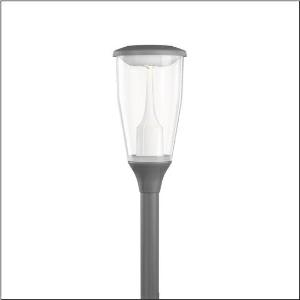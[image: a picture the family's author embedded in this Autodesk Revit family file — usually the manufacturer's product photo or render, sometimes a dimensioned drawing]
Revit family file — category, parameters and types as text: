
# Revit family: dl_11_iq___st1_2a_5xa5575af14hp00022_5e00
name_source: partatom
category: Lighting Fixtures
units: mm (PartAtom-declared; Revit-internal decimal feet)

## family parameters
Cut with Voids When Loaded = No
Host = Face
Light Source = No
Part Type = Normal
Room Calculation Point = No
Round Connector Dimension = Use Diameter
Shared = No

## types (1)
- --- (1 x LED, 4000 lm, 33.6 W, 2200K)
    Apparent Load = 34 VA
    CIE Flux Codes = 33 63 91 94 100
    Color Rendering = 70
    Color Temperature = 2200K
    Default Elevation = 1800 mm
    Description = DL 11 iQ, mast luminaire, Module 540 iQ-SR, primary light control with 3 zone facetted reflector, of plastic, silver coated, highly specular, structured, primary optical cover: cover, of PMMA, transparent, light distribution: ST1.2a, light emission: direct distribution, primary light characteristic: asymmetric, installation type: post-top, LED, High Power LED, rated luminous flux: 4.000lm, luminous efficacy: 119lm/W, light colour: 722, colour temperature: 2200K, control: Street-Remote, Auto-Match, Temp-Guard, Lumen-Switch, Night-Set, Smart-Wire, Light-Fading, Desk-Remote (wireless, voltage-free reading and setting of iQ features in the workshop via application-optimized NFC function/RFID function), optimised constant luminous flux control (CLO 2.0), mains connection: 220..240V, AC, 50/60Hz, connection cable pre-assembled, cable length: 5,5m, start of lifetime: 34W, end of service life: 36W, reduction: 15W, luminaire housing, upper part, of diecast aluminium, coated, Siteco® metallic grey (DB 702S), spigot size: 76mm (post-top), post-top mast mounting element, of diecast aluminium, coated, Siteco® metallic grey (DB 702S), Module 540 iQ-SR, traffic white (RAL 9016), equipment: Power, protection rating (complete): IP66, insulation class (complete): insulation class II (safety insulation), certification: CE, ENEC, ENEC+, VDE, packaging unit: 1 piece

Light Distribution: ST1.2a
    Height = 665 mm
    Lamp = 1 x LED
    Lamp Light Flux = 4000 lm
    Lamp Power = 33.6 W
    Lamp count = 1
    Length = 334 mm
    Luminous efficacy = 119 lm/W
    Manufacturer = Siteco
    ModVariant = No
    Model = 5XA5575AF14HP00022
    Number of Poles = 1
    OnlyDefault = Yes
    Power Factor = 1
    Product Name = DL 11 iQ | ST1.2a
    Product group = mast luminaire | pylon top
    ProductGroupID = 6100
    Protection Class = Protection class II
    Protection Degree = IP 66
    RLX_Detail_Level = 1
    RLX_Emergency_Light_Flux = 0 lm
    RLX_Emergency_Type = 0
    RLX_Emergency_Type_DB = No
    RlxData = <blob elided: 97469 chars, md5=3734c2d8>
    Socket = socket
    Standby Power = 0 W
    System Light Flux = 4000 lm
    System Power = 34 W
    Type Comments = factory setting: luminous flux: 100 % | dim-lin: 254 | 695 mA
    Type Image = l_1258354.jpg
    URL = http://relux.com
    VarID = @adj_002575
    Voltage = 0 V
    Weight = 0.00 kg
    Width = 0 mm  [stored 0 ft]

note: [stored X ft] marks values corroborated as IEEE doubles in the binary element streams (Revit-internal decimal feet)

## geometry (parser evidence)
native form markers: Blend x4, Sweep x15
no freeform markers — native parametric forms only
